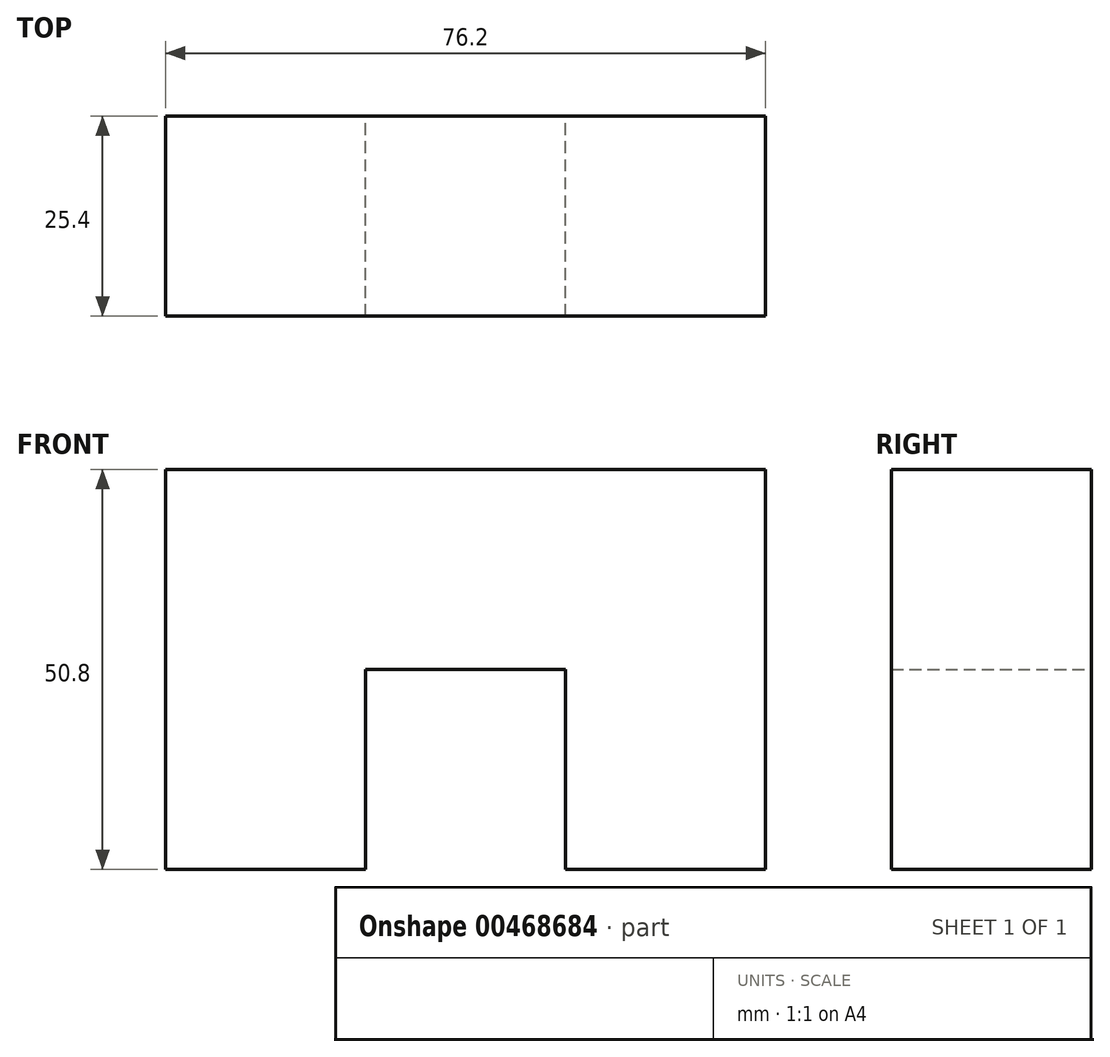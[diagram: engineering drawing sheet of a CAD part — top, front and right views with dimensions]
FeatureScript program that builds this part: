
annotation { "Feature Type Name" : "Feature", "Feature Type Description" : "" }
export const myFeature = defineFeature(function(context is Context, id is Id, definition is map)
    precondition{}
    {
        {
            var Q0;
            Q0=qCreatedBy(makeId("Front.planeOp"),FACE);
            var sketch = newSketch(context, id + "F0", { "sketchPlane" : qUnion([Q0])});
            skLineSegment(sketch, "E0.bottom", {"start": v(-70.45, -51.03) * mm, "end": v(-45.05, -51.03) * mm});
            skLineSegment(sketch, "E0.top", {"start": v(-70.45, -0.23) * mm, "end": v(-45.05, -0.23) * mm});
            skLineSegment(sketch, "E0.left", {"start": v(-70.45, -51.03) * mm, "end": v(-70.45, -0.23) * mm});
            skLineSegment(sketch, "E1.bottom", {"start": v(-45.05, -0.23) * mm, "end": v(5.75, -0.23) * mm});
            skLineSegment(sketch, "E1.right", {"start": v(5.75, -0.23) * mm, "end": v(5.75, -24.03) * mm});
            skLineSegment(sketch, "E2.top", {"start": v(5.75, -51.03) * mm, "end": v(-19.65, -51.03) * mm});
            skLineSegment(sketch, "E2.left", {"start": v(5.75, -24.03) * mm, "end": v(5.75, -51.03) * mm});
            skLineSegment(sketch, "E2.right", {"start": v(-19.65, -25.63) * mm, "end": v(-19.65, -51.03) * mm});
            skLineSegment(sketch, "E3", {"start": v(-45.05, -25.63) * mm, "end": v(-19.65, -25.63) * mm});
            skLineSegment(sketch, "E4", {"start": v(-45.05, -25.63) * mm, "end": v(-45.05, -51.03) * mm});
            skSolve(sketch);
        }
        {
            var Q0;
            Q0=makeQuery(id+"F0.imprint","IMPRINT",FACE,{"disambiguationData":[TD([[makeQuery(id+"F0.imprint","IMPRINT",EDGE,{"derivedFrom":sQuery(id+"F0.wireOp",EDGE,"E0.bottom")}),1.0]])]});
            extrude(context, id + "F1", {"entities" : qUnion([Q0]), "depth" : 25.4 * mm});
        }
    });
